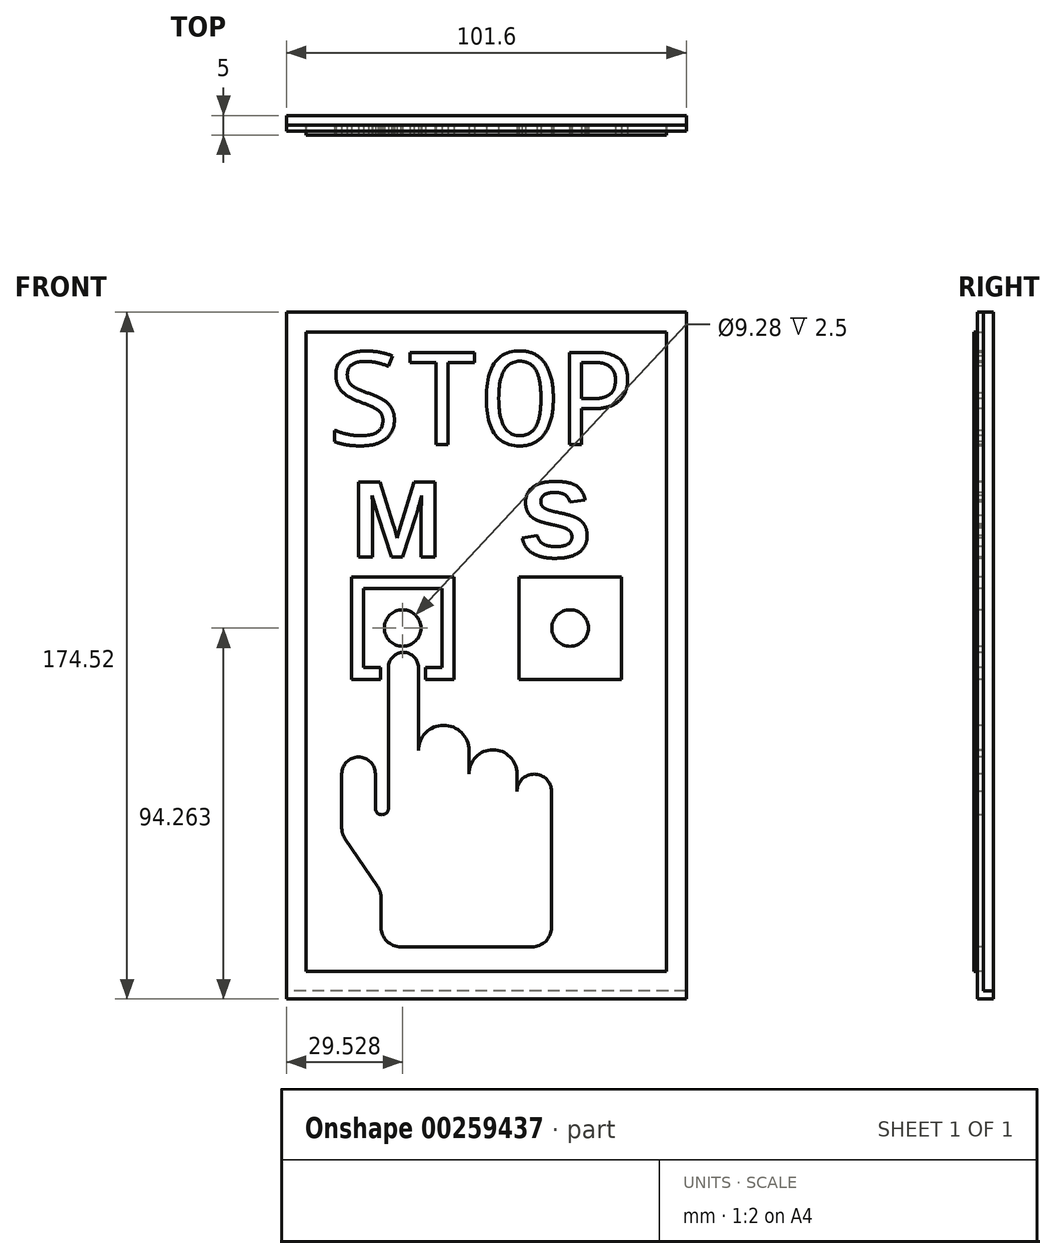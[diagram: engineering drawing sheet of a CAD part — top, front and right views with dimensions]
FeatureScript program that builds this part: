
annotation { "Feature Type Name" : "Feature", "Feature Type Description" : "" }
export const myFeature = defineFeature(function(context is Context, id is Id, definition is map)
    precondition{}
    {
        {
            var Q0;
            Q0=qCreatedBy(makeId("Front.planeOp"),FACE);
            var sketch = newSketch(context, id + "F0", { "sketchPlane" : qUnion([Q0])});
            skLineSegment(sketch, "E0.bottom", {"start": v(0, 0) * mm, "end": v(101.6, 0) * mm});
            skLineSegment(sketch, "E0.top", {"start": v(0, 203.2) * mm, "end": v(101.6, 203.2) * mm});
            skLineSegment(sketch, "E0.left", {"start": v(0, 0) * mm, "end": v(0, 203.2) * mm});
            skLineSegment(sketch, "E0.right", {"start": v(101.6, 0) * mm, "end": v(101.6, 203.2) * mm});
            skLineSegment(sketch, "E1.0", {"start": v(5, 5) * mm, "end": v(5, 198.2) * mm});
            skLineSegment(sketch, "E1.1", {"start": v(5, 5) * mm, "end": v(96.6, 5) * mm});
            skLineSegment(sketch, "E1.2", {"start": v(96.6, 5) * mm, "end": v(96.6, 198.2) * mm});
            skLineSegment(sketch, "E1.3", {"start": v(5, 198.2) * mm, "end": v(96.6, 198.2) * mm});
            skSolve(sketch);
        }
        {
            var Q0;
            Q0=makeQuery(id+"F0.imprint","IMPRINT",FACE,{"disambiguationData":[TD([[makeQuery(id+"F0.imprint","IMPRINT",EDGE,{"derivedFrom":sQuery(id+"F0.wireOp",EDGE,"E1.0")}),-1.0]])]});
            extrude(context, id + "F1", {"entities" : qUnion([Q0]), "depth" : 5 * mm, "offsetDistance" : 25 * mm});
        }
        {
            var Q0;
            Q0=makeQuery(id+"F0.imprint","IMPRINT",FACE,{"disambiguationData":[TD([[makeQuery(id+"F0.imprint","IMPRINT",EDGE,{"derivedFrom":sQuery(id+"F0.wireOp",EDGE,"E0.bottom")}),1.0]])]});
            extrude(context, id + "F2", {"entities" : qUnion([Q0]), "operationType" : NewBodyOperationType.ADD, "depth" : 2.5 * mm, "offsetDistance" : 25 * mm});
        }
        {
            var Q0;
            Q0=makeQuery(id+"F1.opExtrude","CAP_FACE",FACE,{"disambiguationData":[OSD([sQuery(id+"F0.wireOp",EDGE,"E1.0"),sQuery(id+"F0.wireOp",EDGE,"E1.1"),sQuery(id+"F0.wireOp",EDGE,"E1.2"),sQuery(id+"F0.wireOp",EDGE,"E1.3")])],"isStart":false});
            var sketch = newSketch(context, id + "F3", { "sketchPlane" : qUnion([Q0])});
            skLineSegment(sketch, "E2.0", {"start": v(10, 10) * mm, "end": v(10, 193.2) * mm, "construction": true});
            skLineSegment(sketch, "E2.1", {"start": v(10, 10) * mm, "end": v(91.6, 10) * mm, "construction": true});
            skLineSegment(sketch, "E2.2", {"start": v(91.6, 10) * mm, "end": v(91.6, 193.2) * mm, "construction": true});
            skLineSegment(sketch, "E2.3", {"start": v(10, 193.2) * mm, "end": v(91.6, 193.2) * mm, "construction": true});
            skText(sketch, "E3", { "text": "STOP", "fontName": "DroidSansMono.ttf"});
            skLineSegment(sketch, "E4.bottom", {"start": v(19.53, 132.94) * mm, "end": v(39.53, 132.94) * mm});
            skLineSegment(sketch, "E4.top", {"start": v(19.53, 112.94) * mm, "end": v(39.53, 112.94) * mm});
            skLineSegment(sketch, "E4.left", {"start": v(19.53, 132.94) * mm, "end": v(19.53, 112.94) * mm});
            skLineSegment(sketch, "E4.right", {"start": v(39.53, 132.94) * mm, "end": v(39.53, 112.94) * mm});
            skPoint(sketch, "E4.middle", {"position": v(29.53, 122.94) * mm});
            skLineSegment(sketch, "E5.0", {"start": v(16.53, 135.94) * mm, "end": v(42.53, 135.94) * mm});
            skLineSegment(sketch, "E5.1", {"start": v(16.53, 135.94) * mm, "end": v(16.53, 109.94) * mm});
            skLineSegment(sketch, "E5.2", {"start": v(16.53, 109.94) * mm, "end": v(42.53, 109.94) * mm});
            skLineSegment(sketch, "E5.3", {"start": v(42.53, 135.94) * mm, "end": v(42.53, 109.94) * mm});
            skCircle(sketch, "E6", {"center": v(29.53, 122.94) * mm, "radius": 4.64 * mm});
            skLineSegment(sketch, "E7", {"start": v(10, 116.25) * mm, "end": v(10, 95.36) * mm});
            skLineSegment(sketch, "E8", {"start": v(24.06, 54.43) * mm, "end": v(24.06, 46.92) * mm});
            skLineSegment(sketch, "E9", {"start": v(29.06, 41.92) * mm, "end": v(57.08, 41.92) * mm});
            skLineSegment(sketch, "E10", {"start": v(57.08, 41.92) * mm, "end": v(62.35, 41.92) * mm});
            skLineSegment(sketch, "E11", {"start": v(67.35, 46.92) * mm, "end": v(67.35, 81.44) * mm});
            skLineSegment(sketch, "E12", {"start": v(25.91, 112.94) * mm, "end": v(25.91, 77.18) * mm});
            skLineSegment(sketch, "E13", {"start": v(23.19, 57.25) * mm, "end": v(14.93, 69.34) * mm});
            skLineSegment(sketch, "E14", {"start": v(14.06, 72.16) * mm, "end": v(14.06, 85.93) * mm});
            skArc(sketch, "E15", {"start": v(22.59, 85.93) * mm, "mid": v(18.32, 90.2) * mm, "end": v(14.06, 85.93) * mm});
            skLineSegment(sketch, "E16", {"start": v(22.59, 85.93) * mm, "end": v(22.59, 77.18) * mm});
            skArc(sketch, "E17", {"start": v(22.59, 77.18) * mm, "mid": v(24.25, 75.52) * mm, "end": v(25.91, 77.18) * mm});
            skArc(sketch, "E18", {"start": v(33.53, 112.94) * mm, "mid": v(29.72, 116.75) * mm, "end": v(25.91, 112.94) * mm});
            skLineSegment(sketch, "E19", {"start": v(33.53, 112.94) * mm, "end": v(33.53, 91.84) * mm});
            skLineSegment(sketch, "E20", {"start": v(23.9, 112.94) * mm, "end": v(23.9, 109.94) * mm});
            skLineSegment(sketch, "E21", {"start": v(35.28, 112.94) * mm, "end": v(35.28, 109.94) * mm});
            skLineSegment(sketch, "E22", {"start": v(50.8, 169.55) * mm, "end": v(50.8, 115.43) * mm, "construction": true});
            skCircle(sketch, "E23.MirrorC", {"center": v(72.07, 122.94) * mm, "radius": 4.64 * mm});
            skLineSegment(sketch, "E24.MirrorCS", {"start": v(59.07, 135.94) * mm, "end": v(59.07, 109.94) * mm});
            skLineSegment(sketch, "E25.MirrorCS", {"start": v(85.07, 109.94) * mm, "end": v(59.07, 109.94) * mm});
            skLineSegment(sketch, "E26.MirrorCS", {"start": v(85.07, 135.94) * mm, "end": v(85.07, 109.94) * mm});
            skLineSegment(sketch, "E27.MirrorCS", {"start": v(85.07, 135.94) * mm, "end": v(59.07, 135.94) * mm});
            skLineSegment(sketch, "E28.MirrorCS", {"start": v(62.07, 132.94) * mm, "end": v(62.07, 112.94) * mm});
            skLineSegment(sketch, "E29.MirrorCS", {"start": v(82.07, 132.94) * mm, "end": v(82.07, 112.94) * mm});
            skLineSegment(sketch, "E30.MirrorCS", {"start": v(82.07, 112.94) * mm, "end": v(62.07, 112.94) * mm});
            skLineSegment(sketch, "E31.MirrorCS", {"start": v(82.07, 132.94) * mm, "end": v(62.07, 132.94) * mm});
            skLineSegment(sketch, "E32.0", {"start": v(16.53, 140.94) * mm, "end": v(42.53, 140.94) * mm, "construction": true});
            skLineSegment(sketch, "E33.MirrorCS", {"start": v(85.07, 140.94) * mm, "end": v(59.07, 140.94) * mm, "construction": true});
            skText(sketch, "E34", { "text": "M", "fontName": "Arimo-Bold.ttf"});
            skText(sketch, "E35", { "text": "S", "fontName": "Arimo-Bold.ttf"});
            skPoint(sketch, "E36.visualSharp", {"position": v(14.06, 70.62) * mm});
            skArc(sketch, "E36.filletArc", {"start": v(14.06, 72.16) * mm, "mid": v(14.28, 70.69) * mm, "end": v(14.93, 69.34) * mm});
            skPoint(sketch, "E37.visualSharp", {"position": v(24.06, 55.98) * mm});
            skArc(sketch, "E37.filletArc", {"start": v(24.06, 54.43) * mm, "mid": v(23.84, 55.9) * mm, "end": v(23.19, 57.25) * mm});
            skPoint(sketch, "E38.visualSharp", {"position": v(24.06, 41.92) * mm});
            skArc(sketch, "E38.filletArc", {"start": v(24.06, 46.92) * mm, "mid": v(25.52, 43.39) * mm, "end": v(29.06, 41.92) * mm});
            skPoint(sketch, "E39.visualSharp", {"position": v(67.35, 41.92) * mm});
            skArc(sketch, "E39.filletArc", {"start": v(62.35, 41.92) * mm, "mid": v(65.89, 43.39) * mm, "end": v(67.35, 46.92) * mm});
            skArc(sketch, "E40", {"start": v(46.37, 91.84) * mm, "mid": v(39.95, 98.25) * mm, "end": v(33.53, 91.84) * mm});
            skLineSegment(sketch, "E41", {"start": v(46.37, 91.84) * mm, "end": v(46.37, 85.93) * mm});
            skArc(sketch, "E42", {"start": v(58.56, 85.93) * mm, "mid": v(52.46, 92.03) * mm, "end": v(46.37, 85.93) * mm});
            skLineSegment(sketch, "E43", {"start": v(58.56, 85.93) * mm, "end": v(58.56, 81.44) * mm});
            skArc(sketch, "E44", {"start": v(67.35, 81.44) * mm, "mid": v(62.96, 85.83) * mm, "end": v(58.56, 81.44) * mm});
            const initialGuessF3  = {"E3": [0.01, 0.16955, 1, 0, 0.02365], "E34": [0.01653, 0.14094, 1, 0, 0.01996], "E35": [0.05907, 0.14094, 1, 0, 0.01986]};
            skSetInitialGuess(sketch, initialGuessF3);
            skSolve(sketch);
        }
        {
            var Q0;
            Q0=makeQuery(id+"F3.imprint","IMPRINT",FACE,{"disambiguationData":[TD([[makeQuery(id+"F3.imprint","IMPRINT",EDGE,{"derivedFrom":sQuery(id+"F3.wireOp",EDGE,"E3.sketch_text.stroke-0")}),-1.0]])]});
            var Q1;
            Q1=makeQuery(id+"F3.imprint","IMPRINT",FACE,{"disambiguationData":[TD([[makeQuery(id+"F3.imprint","IMPRINT",EDGE,{"derivedFrom":sQuery(id+"F3.wireOp",EDGE,"E3.sketch_text.stroke-20")}),-1.0]])]});
            var Q2;
            Q2=makeQuery(id+"F3.imprint","IMPRINT",FACE,{"disambiguationData":[TD([[makeQuery(id+"F3.imprint","IMPRINT",EDGE,{"derivedFrom":sQuery(id+"F3.wireOp",EDGE,"bff1b2f7-5b43-40db-ad50-737210fc3e16.sketch_text.stroke-0")}),-1.0]])]});
            var Q3;
            Q3=makeQuery(id+"F3.imprint","IMPRINT",FACE,{"disambiguationData":[TD([[makeQuery(id+"F3.imprint","IMPRINT",EDGE,{"derivedFrom":sQuery(id+"F3.wireOp",EDGE,"bff1b2f7-5b43-40db-ad50-737210fc3e16.sketch_text.stroke-35")}),-1.0]])]});
            var Q4;
            Q4=makeQuery(id+"F3.imprint","IMPRINT",FACE,{"disambiguationData":[TD([[makeQuery(id+"F3.imprint","IMPRINT",EDGE,{"derivedFrom":sQuery(id+"F3.wireOp",EDGE,"bff1b2f7-5b43-40db-ad50-737210fc3e16.sketch_text.stroke-60")}),-1.0]])]});
            var Q5;
            Q5=makeQuery(id+"F3.imprint","IMPRINT",FACE,{"disambiguationData":[TD([[makeQuery(id+"F3.imprint","IMPRINT",EDGE,{"derivedFrom":sQuery(id+"F3.wireOp",EDGE,"bff1b2f7-5b43-40db-ad50-737210fc3e16.sketch_text.stroke-72")}),-1.0]])]});
            var Q6;
            Q6=makeQuery(id+"F3.imprint","IMPRINT",FACE,{"disambiguationData":[TD([[makeQuery(id+"F3.imprint","IMPRINT",EDGE,{"derivedFrom":sQuery(id+"F3.wireOp",EDGE,"E3.sketch_text.stroke-28")}),-1.0]])]});
            var Q7;
            Q7=makeQuery(id+"F3.imprint","IMPRINT",FACE,{"disambiguationData":[TD([[makeQuery(id+"F3.imprint","IMPRINT",EDGE,{"derivedFrom":sQuery(id+"F3.wireOp",EDGE,"E3.sketch_text.stroke-40")}),-1.0]])]});
            var Q8;
            Q8=makeQuery(id+"F3.imprint","IMPRINT",FACE,{"disambiguationData":[TD([[makeQuery(id+"F3.imprint","IMPRINT",EDGE,{"derivedFrom":sQuery(id+"F3.wireOp",EDGE,"E8")}),1.0]])]});
            var Q9;
            Q9=makeQuery(id+"F3.imprint","IMPRINT",FACE,{"disambiguationData":[TD([[makeQuery(id+"F3.imprint","IMPRINT",EDGE,{"derivedFrom":sQuery(id+"F3.wireOp",EDGE,"bff1b2f7-5b43-40db-ad50-737210fc3e16.sketch_text.stroke-20")}),-1.0]])]});
            var Q10;
            Q10=makeQuery(id+"F3.imprint","IMPRINT",FACE,{"disambiguationData":[TD([[makeQuery(id+"F3.imprint","IMPRINT",EDGE,{"derivedFrom":sQuery(id+"F3.wireOp",EDGE,"bff1b2f7-5b43-40db-ad50-737210fc3e16.sketch_text.stroke-45")}),-1.0]])]});
            var Q11;
            Q11=makeQuery(id+"F3.imprint","IMPRINT",FACE,{"disambiguationData":[TD([[makeQuery(id+"F3.imprint","IMPRINT",EDGE,{"derivedFrom":sQuery(id+"F3.wireOp",EDGE,"E4.bottom")}),1.0]])]});
            var Q12;
            {var subQ1=sQuery(id+"F3.wireOp",EDGE,"E12");var subQ6=sQuery(id+"F3.wireOp",EDGE,"E5.2");var subQ7=makeQuery(id+"F3.imprint","INTERSECT",VERTEX,{"derivedFrom":[subQ6,subQ1]});Q12=makeQuery(id+"F3.imprint","IMPRINT",FACE,{"disambiguationData":[TD([[makeQuery(id+"F3.imprint","IMPRINT",EDGE,{"disambiguationData":[TD([[subQ7,-1.0]])],"derivedFrom":subQ6}),1.0]])]});}
            var Q13;
            Q13=makeQuery(id+"F3.imprint","IMPRINT",FACE,{"disambiguationData":[TD([[makeQuery(id+"F3.imprint","IMPRINT",EDGE,{"derivedFrom":sQuery(id+"F3.wireOp",EDGE,"E6")}),1.0]])]});
            var Q14;
            {var subQ0=sQuery(id+"F3.wireOp",EDGE,"E18");Q14=makeQuery(id+"F3.imprint","IMPRINT",FACE,{"disambiguationData":[TD([[makeQuery(id+"F3.imprint","IMPRINT",EDGE,{"derivedFrom":subQ0}),1.0]])]});}
            var Q15;
            Q15=makeQuery(id+"F3.imprint","IMPRINT",FACE,{"disambiguationData":[TD([[makeQuery(id+"F3.imprint","IMPRINT",EDGE,{"derivedFrom":sQuery(id+"F3.wireOp",EDGE,"E24.MirrorCS")}),1.0]])]});
            var Q16;
            Q16=makeQuery(id+"F3.imprint","IMPRINT",FACE,{"disambiguationData":[TD([[makeQuery(id+"F3.imprint","IMPRINT",EDGE,{"derivedFrom":sQuery(id+"F3.wireOp",EDGE,"E23.MirrorC")}),-1.0]])]});
            var Q17;
            Q17=makeQuery(id+"F3.imprint","IMPRINT",FACE,{"disambiguationData":[TD([[makeQuery(id+"F3.imprint","IMPRINT",EDGE,{"derivedFrom":sQuery(id+"F3.wireOp",EDGE,"E34.sketch_text.stroke-0")}),-1.0]])]});
            var Q18;
            Q18=makeQuery(id+"F3.imprint","IMPRINT",FACE,{"disambiguationData":[TD([[makeQuery(id+"F3.imprint","IMPRINT",EDGE,{"derivedFrom":sQuery(id+"F3.wireOp",EDGE,"E35.sketch_text.stroke-0")}),-1.0]])]});
            extrude(context, id + "F4", {"entities" : qUnion([Q0, Q1, Q2, Q3, Q4, Q5, Q6, Q7, Q8, Q9, Q10, Q11, Q12, Q13, Q14, Q15, Q16, Q17, Q18]), "operationType" : NewBodyOperationType.REMOVE, "oppositeDirection" : true, "depth" : 2.5 * mm, "offsetDistance" : 25 * mm});
        }
        {
            var Q0;
            {var subQ7=sQuery(id+"F0.wireOp",EDGE,"E1.1");var subQ8=sQuery(id+"F0.wireOp",EDGE,"E1.0");var subQ10=sQuery(id+"F0.wireOp",EDGE,"E1.2");var subQ11=sQuery(id+"F0.wireOp",EDGE,"E1.3");Q0=makeQuery(id+"F4.boolean.opBoolean","SPLIT",FACE,{"disambiguationData":[TD([makeQuery(id+"F1.opExtrude","SWEPT_FACE",FACE,{"disambiguationData":[OSD([subQ8])]})])],"derivedFrom":makeQuery(id+"F1.opExtrude","CAP_FACE",FACE,{"disambiguationData":[OSD([subQ8,subQ7,subQ10,subQ11])],"isStart":false})});}
            var sketch = newSketch(context, id + "F5", { "sketchPlane" : qUnion([Q0])});
            skLineSegment(sketch, "E45", {"start": v(0, 35.74) * mm, "end": v(102.67, 35.74) * mm});
            skLineSegment(sketch, "E46", {"start": v(102.67, 35.74) * mm, "end": v(102.67, 0) * mm});
            skLineSegment(sketch, "E47", {"start": v(102.67, 0) * mm, "end": v(-3.36, 0) * mm});
            skLineSegment(sketch, "E48", {"start": v(-3.36, 0) * mm, "end": v(0, 35.74) * mm});
            skSolve(sketch);
        }
        {
            var Q0;
            Q0 = qSketchRegion(id + "F5", true);
            extrude(context, id + "F6", {"entities" : qUnion([Q0]), "operationType" : NewBodyOperationType.REMOVE, "oppositeDirection" : true, "depth" : 2.5 * mm, "offsetDistance" : 25 * mm});
        }
        {
            var Q0;
            Q0=makeQuery(id+"F6.boolean.opBoolean","MERGE",FACE,{"derivedFrom":[makeQuery(id+"F2.opExtrude","CAP_FACE",FACE,{"disambiguationData":[OSD([sQuery(id+"F0.wireOp",EDGE,"E0.bottom"),sQuery(id+"F0.wireOp",EDGE,"E0.top"),sQuery(id+"F0.wireOp",EDGE,"E0.left"),sQuery(id+"F0.wireOp",EDGE,"E0.right"),sQuery(id+"F0.wireOp",EDGE,"E1.0"),sQuery(id+"F0.wireOp",EDGE,"E1.1"),sQuery(id+"F0.wireOp",EDGE,"E1.2"),sQuery(id+"F0.wireOp",EDGE,"E1.3")])],"isStart":false}),makeQuery(id+"F6.opExtrude","CAP_FACE",FACE,{"disambiguationData":[OSD([sQuery(id+"F5.wireOp",EDGE,"E45"),sQuery(id+"F5.wireOp",EDGE,"E46"),sQuery(id+"F5.wireOp",EDGE,"E47"),sQuery(id+"F5.wireOp",EDGE,"E48")])],"isStart":false})]});
            var sketch = newSketch(context, id + "F7", { "sketchPlane" : qUnion([Q0])});
            skLineSegment(sketch, "E49", {"start": v(5, 35.74) * mm, "end": v(5, 30.74) * mm});
            skLineSegment(sketch, "E50", {"start": v(5, 30.74) * mm, "end": v(0, 30.74) * mm});
            skLineSegment(sketch, "E51", {"start": v(0, 30.74) * mm, "end": v(0, 0) * mm});
            skLineSegment(sketch, "E52", {"start": v(0, 0) * mm, "end": v(101.6, 0) * mm});
            skLineSegment(sketch, "E53", {"start": v(101.6, 0) * mm, "end": v(101.6, 30.74) * mm});
            skLineSegment(sketch, "E54", {"start": v(101.6, 30.74) * mm, "end": v(5, 30.74) * mm});
            skSolve(sketch);
        }
        {
            var Q0;
            Q0 = qSketchRegion(id + "F7", true);
            extrude(context, id + "F8", {"entities" : qUnion([Q0]), "operationType" : NewBodyOperationType.REMOVE, "endBound" : BoundingType.THROUGH_ALL, "oppositeDirection" : true, "depth" : 25 * mm, "offsetDistance" : 25 * mm, "hasSecondDirection" : true, "secondDirectionBound" : BoundingType.THROUGH_ALL, "secondDirectionOppositeDirection" : false, "secondDirectionDepth" : 25 * mm});
        }
        {
            var Q0;
            Q0=makeQuery(id+"F0.imprint","IMPRINT",FACE,{"disambiguationData":[TD([[makeQuery(id+"F0.imprint","IMPRINT",EDGE,{"derivedFrom":sQuery(id+"F0.wireOp",EDGE,"E0.bottom")}),1.0]])]});
            var Q1;
            Q1=makeQuery(id+"F0.imprint","IMPRINT",FACE,{"disambiguationData":[TD([[makeQuery(id+"F0.imprint","IMPRINT",EDGE,{"derivedFrom":sQuery(id+"F0.wireOp",EDGE,"E1.0")}),-1.0]])]});
            extrude(context, id + "F9", {"entities" : qUnion([Q0, Q1]), "depth" : 4 * mm, "offsetDistance" : 25 * mm});
        }
        {
            var Q0;
            Q0=makeQuery(id+"F9.opExtrude","CAP_FACE",FACE,{"disambiguationData":[OSD([sQuery(id+"F0.wireOp",EDGE,"E0.bottom"),sQuery(id+"F0.wireOp",EDGE,"E0.top"),sQuery(id+"F0.wireOp",EDGE,"E0.left"),sQuery(id+"F0.wireOp",EDGE,"E0.right")])],"isStart":false});
            var sketch = newSketch(context, id + "F10", { "sketchPlane" : qUnion([Q0])});
            skLineSegment(sketch, "E55.bottom", {"start": v(0, 0) * mm, "end": v(101.6, 0) * mm});
            skLineSegment(sketch, "E55.top", {"start": v(0, 28.68) * mm, "end": v(101.6, 28.68) * mm});
            skLineSegment(sketch, "E55.left", {"start": v(0, 0) * mm, "end": v(0, 28.68) * mm});
            skLineSegment(sketch, "E55.right", {"start": v(101.6, 0) * mm, "end": v(101.6, 28.68) * mm});
            skSolve(sketch);
        }
        {
            var Q0;
            Q0 = qSketchRegion(id + "F10", true);
            extrude(context, id + "F11", {"entities" : qUnion([Q0]), "operationType" : NewBodyOperationType.REMOVE, "oppositeDirection" : true, "depth" : 25 * mm, "offsetDistance" : 25 * mm});
        }
    });
